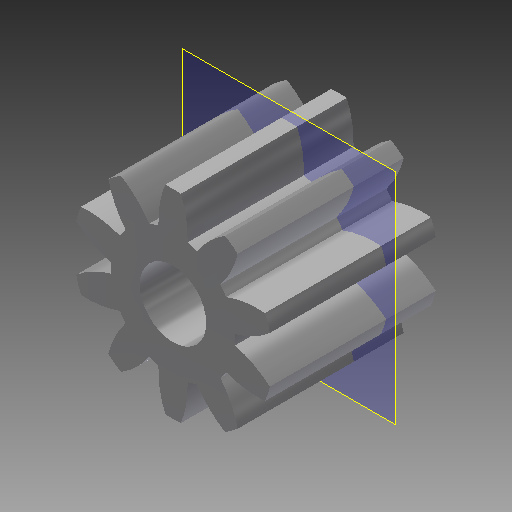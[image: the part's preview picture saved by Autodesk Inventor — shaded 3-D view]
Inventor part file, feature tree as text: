
AUTODESK INVENTOR PART (.ipt)
format: ipt  version: 2017 (Build 210142000, 142)  size: 210,432 bytes
history: native  units: mm (DEFAULTED — no unit token found)
features: plane x4, other x3, sketch x3, extrude x2
ambient origin geometry x8: Origin, YZ Plane, XZ Plane, XY Plane, X Axis, Y Axis, Z Axis, Center Point
bodies: Solid1 (feature_tree)
feature tree (12):
  extrude  "Extrusion1"  Depth=5.0mm TaperAngle=0.0deg
  plane  "Work Plane2"
  plane  "Work Plane8"
  plane  "Work Plane9"
  other  "Spur Gear"
  extrude  "Extrusion2"  Depth=10.0mm TaperAngle=0.0deg
  plane  "Work Plane12"
  sketch  "Sketch1"  dims[d0=6.0mm d1=5.0mm d2=0.0mm]
  sketch  "Sketch2"  dims[d3=5.0mm d4=10.0mm d5=0.0mm]
  other  "Srf1"
  sketch  "Sketch3"  dims[d16=12.0mm d17=0.0mm d34=3.141593mm d39=0.0mm d41=0.0mm d43=12.0mm d46=12.0mm d47=0.0mm d48=0.0mm d49=2.0mm d50=10.0mm d51=0.0mm d53=-1.5mm]
  other  "Pitch Diameter"
